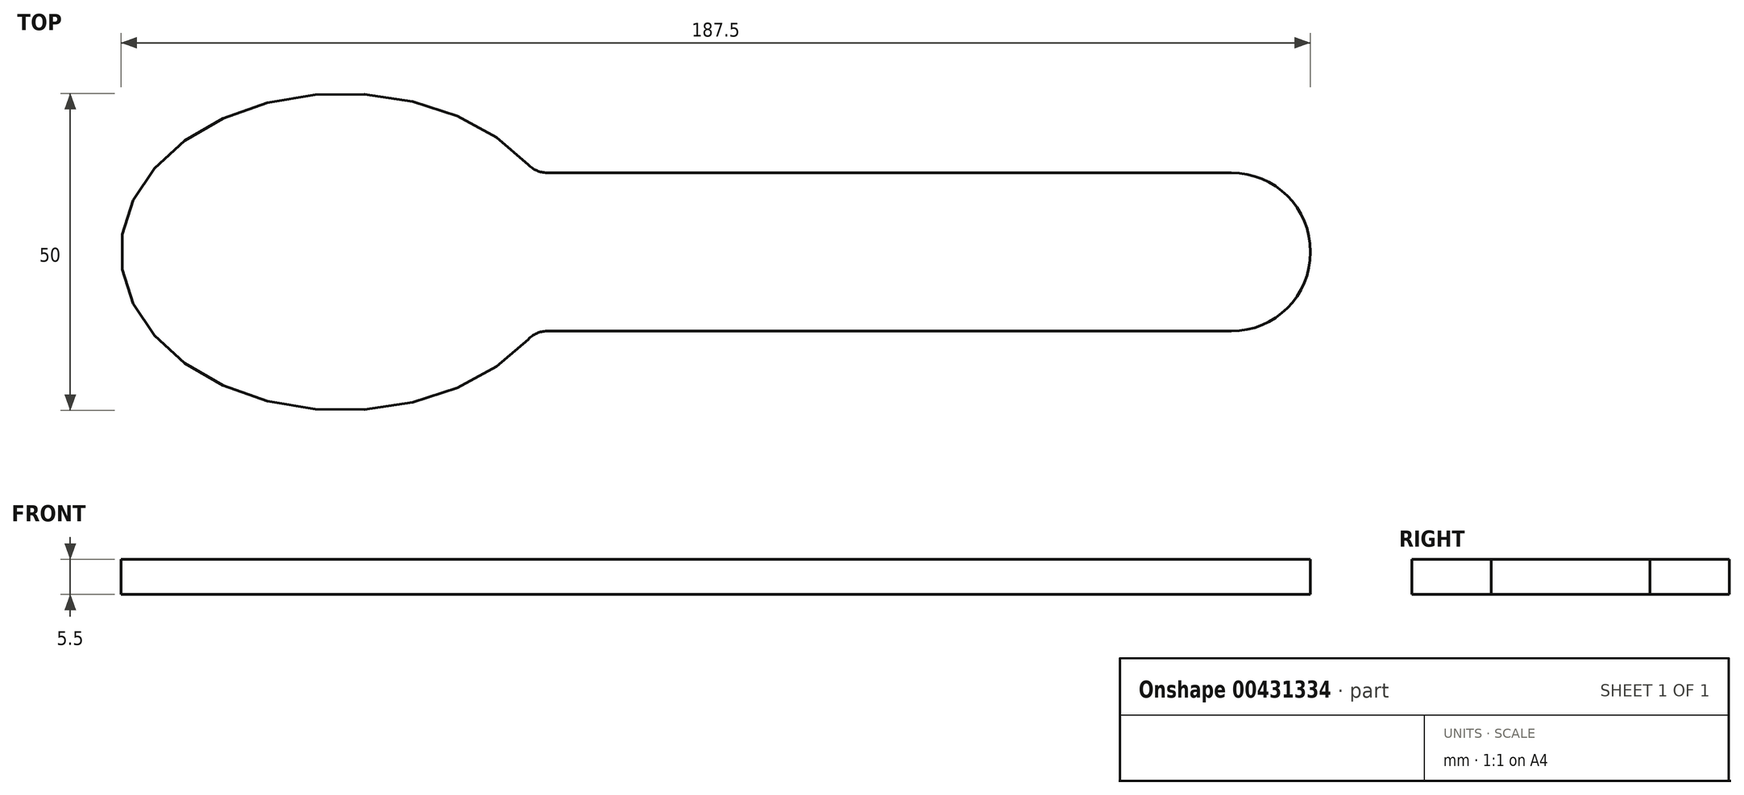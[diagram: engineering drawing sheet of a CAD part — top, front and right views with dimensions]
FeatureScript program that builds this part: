
annotation { "Feature Type Name" : "Feature", "Feature Type Description" : "" }
export const myFeature = defineFeature(function(context is Context, id is Id, definition is map)
    precondition{}
    {
        {
            var Q0;
            Q0=qCreatedBy(makeId("Top.planeOp"),FACE);
            var sketch = newSketch(context, id + "F0", { "sketchPlane" : qUnion([Q0])});
            skLineSegment(sketch, "E0", {"start": v(0, 45.6) * mm, "end": v(0, -45.6) * mm, "construction": true});
            skLineSegment(sketch, "E1", {"start": v(-87.5, 0) * mm, "end": v(87.5, 0) * mm, "construction": true});
            skEllipticalArc(sketch, "E2", {});
            skLineSegment(sketch, "E3", {"start": v(-52.5, 0) * mm, "end": v(-17.5, 0) * mm, "construction": true});
            skLineSegment(sketch, "E4", {"start": v(-52.5, 0) * mm, "end": v(-52.5, 25) * mm, "construction": true});
            skLineSegment(sketch, "E5", {"start": v(-22.19, 12.5) * mm, "end": v(87.5, 12.5) * mm});
            skArc(sketch, "E6", {"start": v(87.5, -12.5) * mm, "mid": v(100, 0) * mm, "end": v(87.5, 12.5) * mm});
            skLineSegment(sketch, "E7", {"start": v(-22.19, -12.5) * mm, "end": v(93.44, -12.5) * mm});
            const initialGuessF0  = {"E2": [-0.0525, 0, 1, 0, 0.035, 0.025, 0.5235987755982993, 5.759586531581288]};
            skSetInitialGuess(sketch, initialGuessF0);
            skSolve(sketch);
        }
        {
            var Q0;
            Q0 = qSketchRegion(id + "F0", true);
            extrude(context, id + "F1", {"entities" : qUnion([Q0]), "depth" : 5.5 * mm});
        }
        {
            var Q0;
            Q0=makeQuery(id+"F1.opExtrude","SWEPT_EDGE",EDGE,{"disambiguationData":[OSD([sQuery(id+"F0.wireOp",EDGE,"E2"),sQuery(id+"F0.wireOp",EDGE,"E5")])]});
            var Q1;
            Q1=makeQuery(id+"F1.opExtrude","SWEPT_EDGE",EDGE,{"disambiguationData":[OSD([sQuery(id+"F0.wireOp",EDGE,"E2"),sQuery(id+"F0.wireOp",EDGE,"E7")])]});
            fillet(context, id + "F2", {"entities" : qUnion([Q0, Q1]), "radius" : 4 * mm, "tangentPropagation" : true, "allowEdgeOverflow" : false});
        }
    });
